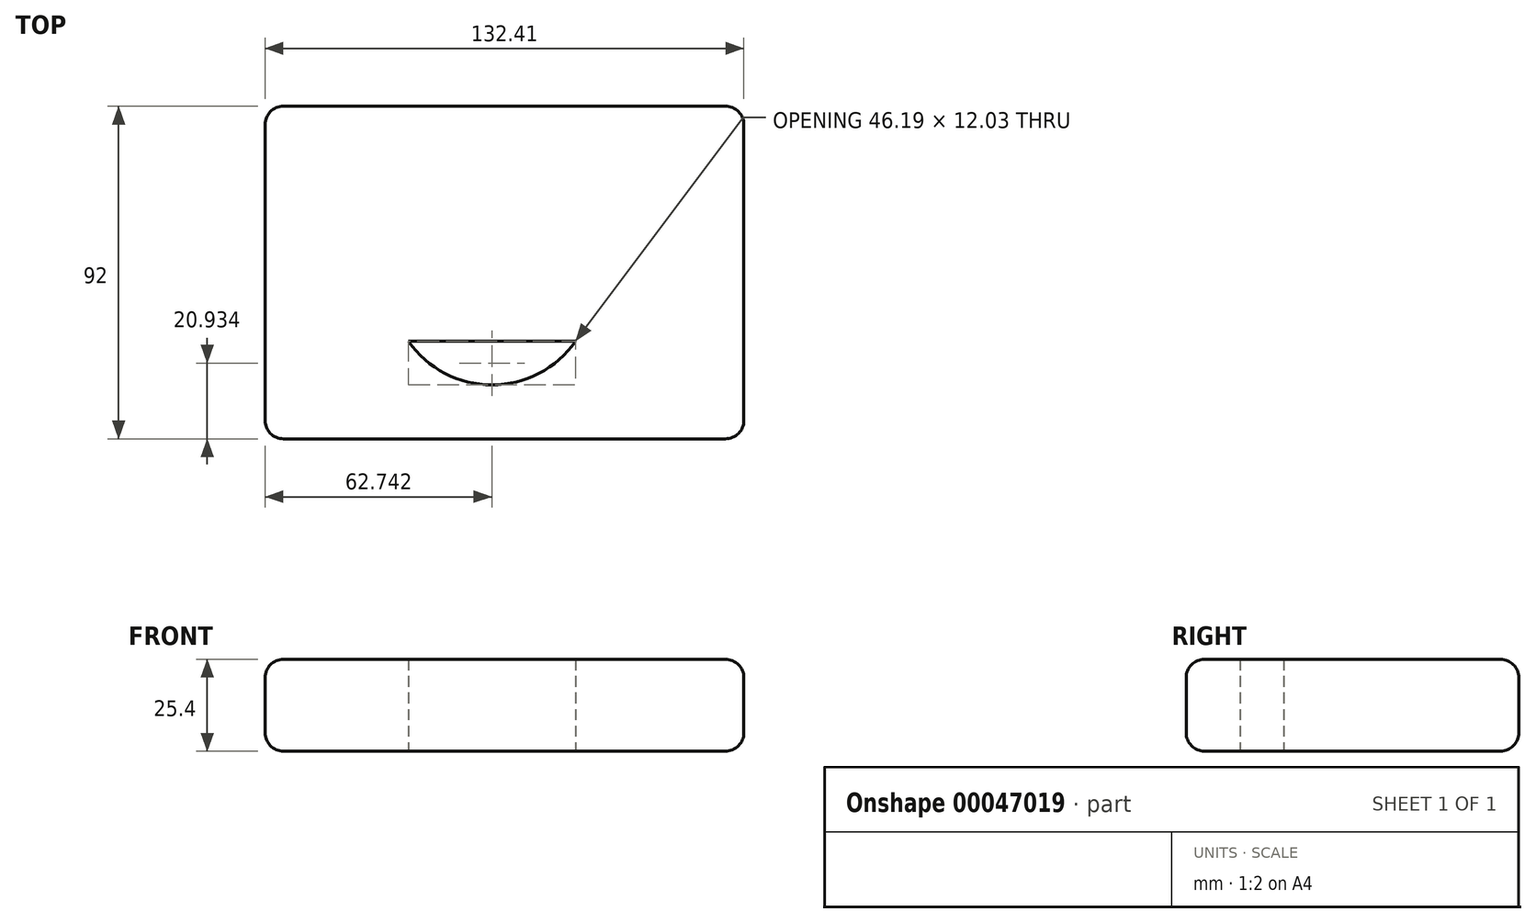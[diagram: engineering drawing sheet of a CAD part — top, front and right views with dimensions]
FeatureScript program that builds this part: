
annotation { "Feature Type Name" : "Feature", "Feature Type Description" : "" }
export const myFeature = defineFeature(function(context is Context, id is Id, definition is map)
    precondition{}
    {
        {
            var Q0;
            Q0=qCreatedBy(makeId("Top.planeOp"),FACE);
            var sketch = newSketch(context, id + "F0", { "sketchPlane" : qUnion([Q0])});
            skLineSegment(sketch, "E0.bottom", {"start": v(-92.38, 35.03) * mm, "end": v(40.03, 35.03) * mm});
            skLineSegment(sketch, "E0.top", {"start": v(-92.38, -56.97) * mm, "end": v(40.03, -56.97) * mm});
            skLineSegment(sketch, "E0.left", {"start": v(-92.38, 35.03) * mm, "end": v(-92.38, -56.97) * mm});
            skLineSegment(sketch, "E0.right", {"start": v(40.03, 35.03) * mm, "end": v(40.03, -56.97) * mm});
            skCircle(sketch, "E1", {"center": v(-29.64, -13.86) * mm, "radius": 28.2 * mm});
            skLineSegment(sketch, "E2", {"start": v(-92.38, 0) * mm, "end": v(40.03, 0) * mm});
            skLineSegment(sketch, "E3", {"start": v(40.03, 0) * mm, "end": v(-26.17, 0) * mm});
            skLineSegment(sketch, "E4", {"start": v(-92.38, -30.02) * mm, "end": v(40.03, -30.02) * mm});
            skPoint(sketch, "E5", {"position": v(-81.78, 26.02) * mm});
            skPoint(sketch, "E6", {"position": v(32.03, 26.58) * mm});
            skPoint(sketch, "E7", {"position": v(32.03, -49.48) * mm});
            skPoint(sketch, "E8", {"position": v(-82.91, -50.42) * mm});
            skSolve(sketch);
        }
        {
            var Q0;
            Q0 = qSketchRegion(id + "F0", true);
            var Q1;
            {var subQ0=sQuery(id+"F0.wireOp",EDGE,"E1");var subQ3=sQuery(id+"F0.wireOp",EDGE,"E2");var subQ4=makeQuery(id+"F0.imprint","INTERSECT",VERTEX,{"derivedFrom":[subQ0,subQ3]});Q1=makeQuery(id+"F0.imprint","IMPRINT",FACE,{"disambiguationData":[TD([[makeQuery(id+"F0.imprint","IMPRINT",EDGE,{"disambiguationData":[TD([[subQ4,-1.0]])],"derivedFrom":subQ0}),1.0]])]});}
            var Q2;
            {var subQ1=sQuery(id+"F0.wireOp",EDGE,"E1");var subQ3=sQuery(id+"F0.wireOp",EDGE,"E2");var subQ5=makeQuery(id+"F0.imprint","INTERSECT",VERTEX,{"derivedFrom":[subQ1,subQ3]});Q2=makeQuery(id+"F0.imprint","IMPRINT",FACE,{"disambiguationData":[TD([[makeQuery(id+"F0.imprint","IMPRINT",EDGE,{"disambiguationData":[TD([[subQ5,1.0]])],"derivedFrom":subQ1}),1.0]])]});}
            var Q3;
            {var subQ0=sQuery(id+"F0.wireOp",EDGE,"E4");var subQ1=sQuery(id+"F0.wireOp",EDGE,"E1");var subQ3=makeQuery(id+"F0.imprint","INTERSECT",VERTEX,{"disambiguationData":[OD(0.0)],"derivedFrom":[subQ1,subQ0]});Q3=makeQuery(id+"F0.imprint","IMPRINT",FACE,{"disambiguationData":[TD([[makeQuery(id+"F0.imprint","IMPRINT",EDGE,{"disambiguationData":[TD([[subQ3,-1.0]])],"derivedFrom":subQ1}),1.0]])]});}
            extrude(context, id + "F1", {"entities" : qUnion([Q0, Q1, Q2, Q3]), "depth" : 25.4 * mm});
        }
        {
            var Q0;
            Q0=makeQuery(id+"F1.opExtrude","SWEPT_FACE",FACE,{"disambiguationData":[OSD([sQuery(id+"F0.wireOp",EDGE,"E0.right")])]});
            var Q1;
            Q1=makeQuery(id+"F1.opExtrude","SWEPT_FACE",FACE,{"disambiguationData":[OSD([sQuery(id+"F0.wireOp",EDGE,"E0.top")])]});
            var Q2;
            Q2=makeQuery(id+"F1.opExtrude","SWEPT_FACE",FACE,{"disambiguationData":[OSD([sQuery(id+"F0.wireOp",EDGE,"E0.bottom")])]});
            var Q3;
            Q3=makeQuery(id+"F1.opExtrude","SWEPT_FACE",FACE,{"disambiguationData":[OSD([sQuery(id+"F0.wireOp",EDGE,"E0.left")])]});
            fillet(context, id + "F2", {"entities" : qUnion([Q0, Q1, Q2, Q3]), "radius" : 5.08 * mm, "tangentPropagation" : true, "allowEdgeOverflow" : false});
        }
    });
